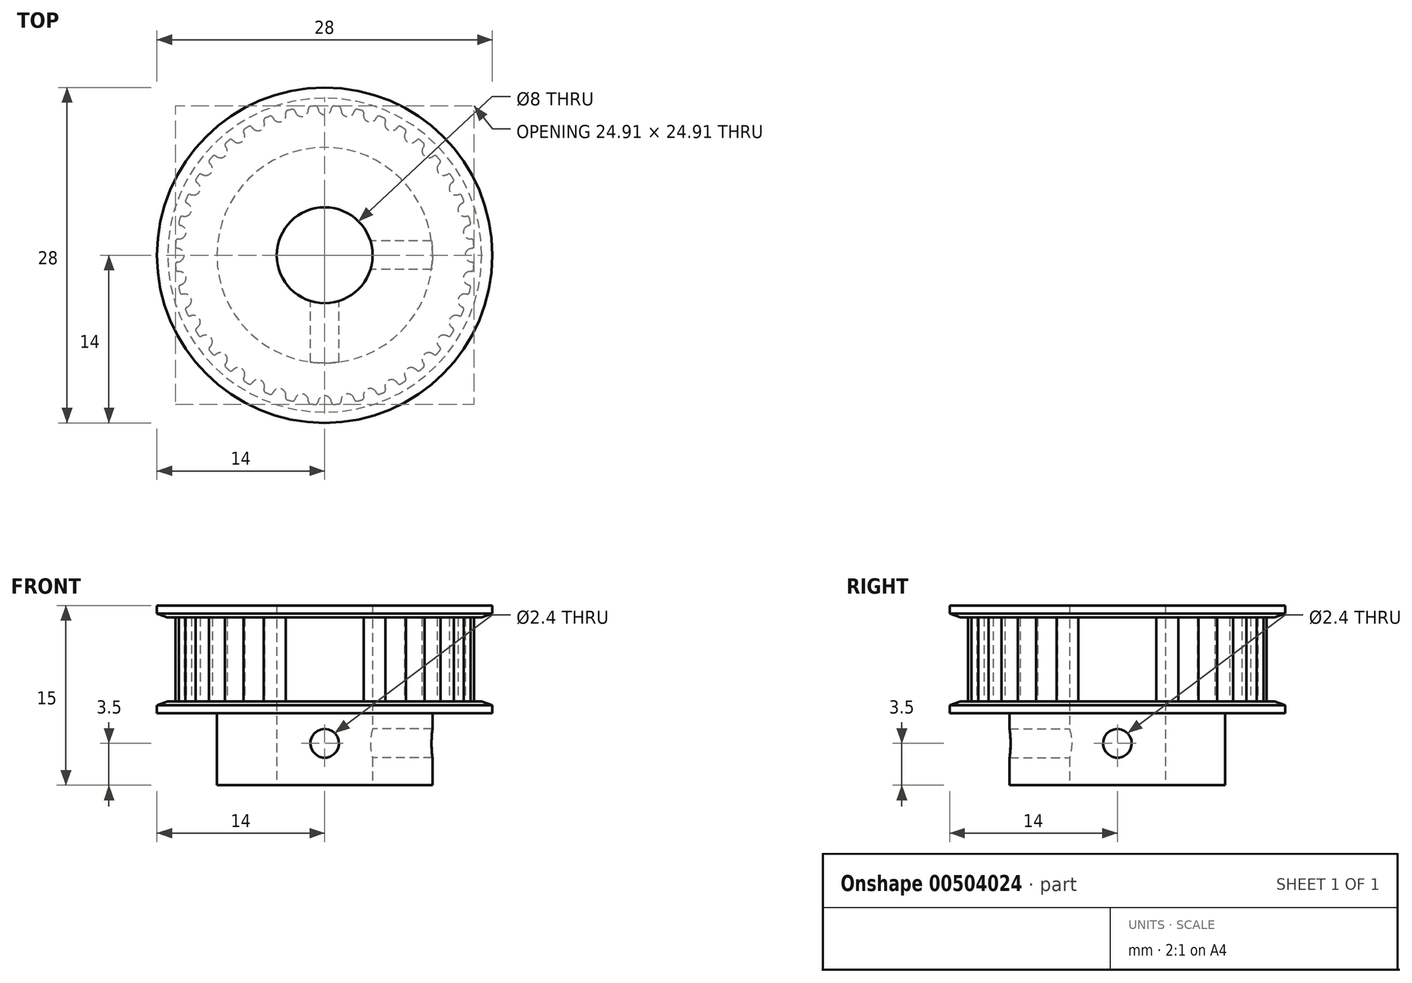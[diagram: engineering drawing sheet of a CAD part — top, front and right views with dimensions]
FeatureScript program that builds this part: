
annotation { "Feature Type Name" : "Feature", "Feature Type Description" : "" }
export const myFeature = defineFeature(function(context is Context, id is Id, definition is map)
    precondition{}
    {
        {
            assignVariable(context, id + "F0", {"name" : "teeth", "anyValue" : 40});
        }
        {
            assignVariable(context, id + "F1", {"name" : "belt_width", "anyValue" : 6 * mm});
        }
        {
            assignVariable(context, id + "F2", {"name" : "bore_diameter", "anyValue" : 8 * mm});
        }
        {
            var Q0;
            Q0=qCreatedBy(makeId("Top.planeOp"),FACE);
            var sketch = newSketch(context, id + "F3", { "sketchPlane" : qUnion([Q0])});
            skLineSegment(sketch, "E0", {"start": v(0, 0) * mm, "end": v(0, 11.73) * mm, "construction": true});
            skCircle(sketch, "E1", {"center": v(0, 0) * mm, "radius": 12.48 * mm});
            skPoint(sketch, "E2.MirrorCS.end.orphan", {"position": v(0.98, 12.44) * mm});
            skLineSegment(sketch, "E3", {"start": v(0.98, 12.44) * mm, "end": v(1, 12.7) * mm, "construction": true});
            skLineSegment(sketch, "E4", {"start": v(-0.98, 12.44) * mm, "end": v(-1, 12.7) * mm, "construction": true});
            skArc(sketch, "E5", {"start": v(0, 11.73) * mm, "mid": v(0.34, 11.84) * mm, "end": v(0.54, 12.14) * mm});
            skArc(sketch, "E6", {"start": v(0.54, 12.14) * mm, "mid": v(0.56, 12.23) * mm, "end": v(0.58, 12.33) * mm, "construction": true});
            skLineSegment(sketch, "E7", {"start": v(0, 11.73) * mm, "end": v(0, 12.48) * mm, "construction": true});
            skLineSegment(sketch, "E8", {"start": v(0, 12.48) * mm, "end": v(0, 12.73) * mm, "construction": true});
            skArc(sketch, "E9", {"start": v(0.58, 12.33) * mm, "mid": v(0.64, 12.42) * mm, "end": v(0.74, 12.46) * mm, "construction": true});
            skArc(sketch, "E10", {"start": v(1, 12.7) * mm, "mid": v(0, 12.73) * mm, "end": v(-1, 12.7) * mm, "construction": true});
            skLineSegment(sketch, "E11", {"start": v(0.98, 12.44) * mm, "end": v(0.92, 11.7) * mm});
            skLineSegment(sketch, "E12", {"start": v(0.92, 11.7) * mm, "end": v(0, 0) * mm});
            skLineSegment(sketch, "E13", {"start": v(0, 0) * mm, "end": v(-0.92, 11.7) * mm});
            skLineSegment(sketch, "E14", {"start": v(-0.92, 11.7) * mm, "end": v(-0.98, 12.44) * mm});
            skArc(sketch, "E15", {"start": v(0.77, 12.45) * mm, "mid": v(0.65, 12.42) * mm, "end": v(0.58, 12.31) * mm});
            skArc(sketch, "E16", {"start": v(0.54, 12.14) * mm, "mid": v(0.56, 12.22) * mm, "end": v(0.58, 12.31) * mm});
            skArc(sketch, "E17.MirrorCS", {"start": v(0, 11.73) * mm, "mid": v(-0.34, 11.84) * mm, "end": v(-0.54, 12.14) * mm});
            skArc(sketch, "E18.MirrorCS", {"start": v(-0.54, 12.14) * mm, "mid": v(-0.56, 12.22) * mm, "end": v(-0.58, 12.31) * mm});
            skArc(sketch, "E19.MirrorCS", {"start": v(-0.77, 12.45) * mm, "mid": v(-0.65, 12.42) * mm, "end": v(-0.58, 12.31) * mm});
            skArc(sketch, "E20", {"start": v(0, 12.48) * mm, "mid": v(-0.2, 12.48) * mm, "end": v(-0.4, 12.47) * mm});
            skArc(sketch, "E21", {"start": v(0.92, 11.7) * mm, "mid": v(0, 11.73) * mm, "end": v(-0.92, 11.7) * mm, "construction": true});
            skLineSegment(sketch, "E22", {"start": v(1, 12.7) * mm, "end": v(1.03, 13.07) * mm, "construction": true});
            skLineSegment(sketch, "E23", {"start": v(-1, 12.7) * mm, "end": v(-1.03, 13.07) * mm, "construction": true});
            skArc(sketch, "E24", {"start": v(-1.03, 13.07) * mm, "mid": v(0, 13.1) * mm, "end": v(1.03, 13.07) * mm, "construction": true});
            skSolve(sketch);
        }
        {
            var Q0;
            Q0=makeQuery(id+"F3.imprint","IMPRINT",FACE,{"disambiguationData":[TD([[makeQuery(id+"F3.imprint","IMPRINT",EDGE,{"derivedFrom":sQuery(id+"F3.wireOp",EDGE,"E5")}),-1.0]])]});
            var Q1;
            {var subQ1=sQuery(id+"F3.wireOp",EDGE,"E14");Q1=makeQuery(id+"F3.imprint","IMPRINT",FACE,{"disambiguationData":[TD([[makeQuery(id+"F3.imprint","IMPRINT",EDGE,{"derivedFrom":subQ1}),-1.0]])]});}
            var Q2;
            {var subQ0=sQuery(id+"F3.wireOp",EDGE,"E12");Q2=makeQuery(id+"F3.imprint","IMPRINT",FACE,{"disambiguationData":[TD([[makeQuery(id+"F3.imprint","IMPRINT",EDGE,{"derivedFrom":subQ0}),-1.0]])]});}
            extrude(context, id + "F4", {"entities" : qUnion([Q0, Q1, Q2]), "depth" : getVariable(context, 'belt_width') + 1 * mm, "symmetric" : true});
        }
        {
            var Q0;
            Q0=makeQuery(id+"F4.opExtrude","SWEPT_BODY",BODY,{"disambiguationData":[OSD([sQuery(id+"F3.wireOp",EDGE,"E1"),sQuery(id+"F3.wireOp",EDGE,"E5"),sQuery(id+"F3.wireOp",EDGE,"E11"),sQuery(id+"F3.wireOp",EDGE,"E12"),sQuery(id+"F3.wireOp",EDGE,"E13"),sQuery(id+"F3.wireOp",EDGE,"E14"),sQuery(id+"F3.wireOp",EDGE,"E15"),sQuery(id+"F3.wireOp",EDGE,"E16"),sQuery(id+"F3.wireOp",EDGE,"E17.MirrorCS"),sQuery(id+"F3.wireOp",EDGE,"E18.MirrorCS"),sQuery(id+"F3.wireOp",EDGE,"E19.MirrorCS")])]});
            var Q1;
            Q1=makeQuery(id+"F4.opExtrude","SWEPT_EDGE",EDGE,{"disambiguationData":[OSD([sQuery(id+"F3.wireOp",EDGE,"E12"),sQuery(id+"F3.wireOp",EDGE,"E13")])]});
            circularPattern(context, id + "F5", {"operationType" : NewBodyOperationType.ADD, "entities" : qUnion([Q0]), "axis" : qUnion([Q1]), "angle" : 360 * degree, "instanceCount" : getVariable(context, 'teeth'), "equalSpace" : true});
        }
        {
            var Q0;
            Q0=qCreatedBy(makeId("Front.planeOp"),FACE);
            var sketch = newSketch(context, id + "F6", { "sketchPlane" : qUnion([Q0])});
            skLineSegment(sketch, "E25", {"start": v(0, -3.5) * mm, "end": v(13.1, -3.5) * mm});
            skLineSegment(sketch, "E26", {"start": v(13.1, -3.5) * mm, "end": v(14, -3.82) * mm});
            skLineSegment(sketch, "E27", {"start": v(9, -10.5) * mm, "end": v(0, -10.5) * mm});
            skLineSegment(sketch, "E28", {"start": v(0, 3.5) * mm, "end": v(13.1, 3.5) * mm});
            skLineSegment(sketch, "E29", {"start": v(14, 3.82) * mm, "end": v(13.1, 3.5) * mm});
            skLineSegment(sketch, "E30", {"start": v(14, 3.82) * mm, "end": v(14, 4.5) * mm});
            skLineSegment(sketch, "E31", {"start": v(14, 4.5) * mm, "end": v(0, 4.5) * mm});
            skLineSegment(sketch, "E32", {"start": v(0, 4.5) * mm, "end": v(0, 3.5) * mm});
            skLineSegment(sketch, "E33", {"start": v(13.1, -3.5) * mm, "end": v(14, -3.5) * mm, "construction": true});
            skLineSegment(sketch, "E34", {"start": v(14, -3.5) * mm, "end": v(14, -3.82) * mm, "construction": true});
            skLineSegment(sketch, "E35", {"start": v(13.1, 3.5) * mm, "end": v(14, 3.5) * mm, "construction": true});
            skLineSegment(sketch, "E36", {"start": v(14, 3.5) * mm, "end": v(14, 3.82) * mm, "construction": true});
            skLineSegment(sketch, "E37", {"start": v(12.48, 0) * mm, "end": v(12.48, -3.5) * mm, "construction": true});
            skLineSegment(sketch, "E38", {"start": v(14, -4.5) * mm, "end": v(0, -4.5) * mm});
            skLineSegment(sketch, "E39", {"start": v(14, -3.82) * mm, "end": v(14, -4.5) * mm});
            skLineSegment(sketch, "E40", {"start": v(0, -3.5) * mm, "end": v(0, -4.5) * mm});
            skLineSegment(sketch, "E41", {"start": v(9, -10.5) * mm, "end": v(9, -4.5) * mm});
            skLineSegment(sketch, "E42", {"start": v(0, -10.5) * mm, "end": v(0, -4.5) * mm});
            skSolve(sketch);
        }
        {
            var Q0;
            Q0=makeQuery(id+"F6.imprint","IMPRINT",FACE,{"disambiguationData":[TD([[makeQuery(id+"F6.imprint","IMPRINT",EDGE,{"derivedFrom":sQuery(id+"F6.wireOp",EDGE,"E28")}),1.0]])]});
            var Q1;
            Q1=makeQuery(id+"F6.imprint","IMPRINT",FACE,{"disambiguationData":[TD([[makeQuery(id+"F6.imprint","IMPRINT",EDGE,{"derivedFrom":sQuery(id+"F6.wireOp",EDGE,"E25")}),-1.0]])]});
            var Q2;
            Q2=makeQuery(id+"F6.imprint","IMPRINT",FACE,{"disambiguationData":[TD([[makeQuery(id+"F6.imprint","IMPRINT",EDGE,{"derivedFrom":sQuery(id+"F6.wireOp",EDGE,"E27")}),-1.0]])]});
            var Q3;
            Q3=qConstructionFilter(qBodyType(qCreatedBy(id+"F6",EDGE),BodyType.WIRE),ConstructionObject.NO);
            var Q4;
            Q4=sQuery(id+"F6.wireOp",EDGE,"E42");
            revolve(context, id + "F7", {"operationType" : NewBodyOperationType.ADD, "entities" : qUnion([Q0, Q1, Q2]), "surfaceEntities" : qUnion([Q3]), "axis" : qUnion([Q4]), "revolveType" : RevolveType.FULL});
        }
        {
            var Q0;
            Q0=makeQuery(id+"F7.opRevolve","SWEPT_FACE",FACE,{"disambiguationData":[OSD([sQuery(id+"F6.wireOp",EDGE,"E27")])]});
            var sketch = newSketch(context, id + "F8", { "sketchPlane" : qUnion([Q0])});
            skPoint(sketch, "E43", {"position": v(0, 0) * mm});
            skSolve(sketch);
        }
        {
            var Q0;
            Q0=sQuery(id+"F8.wireOp",VERTEX,"E43");
            var Q1;
            Q1=makeQuery(id+"F4.opExtrude","SWEPT_BODY",BODY,{"disambiguationData":[OSD([sQuery(id+"F3.wireOp",EDGE,"E1"),sQuery(id+"F3.wireOp",EDGE,"E5"),sQuery(id+"F3.wireOp",EDGE,"E11"),sQuery(id+"F3.wireOp",EDGE,"E12"),sQuery(id+"F3.wireOp",EDGE,"E13"),sQuery(id+"F3.wireOp",EDGE,"E14"),sQuery(id+"F3.wireOp",EDGE,"E15"),sQuery(id+"F3.wireOp",EDGE,"E16"),sQuery(id+"F3.wireOp",EDGE,"E17.MirrorCS"),sQuery(id+"F3.wireOp",EDGE,"E18.MirrorCS"),sQuery(id+"F3.wireOp",EDGE,"E19.MirrorCS")])]});
            hole(context, id + "F9", {"style" : HoleStyle.SIMPLE, "holeDiameter" : getVariable(context, 'bore_diameter'), "endStyle" : HoleEndStyle.THROUGH, "locations" : qUnion([Q0]), "scope" : qUnion([Q1]), "isTappedThrough" : true});
        }
        {
            var Q0;
            Q0=qCreatedBy(makeId("Front.planeOp"),FACE);
            var sketch = newSketch(context, id + "F10", { "sketchPlane" : qUnion([Q0])});
            skPoint(sketch, "E44", {"position": v(0, -7) * mm});
            skLineSegment(sketch, "E45", {"start": v(0, -10.5) * mm, "end": v(0, -3.5) * mm});
            skSolve(sketch);
        }
        {
            var Q0;
            Q0=qCreatedBy(makeId("Right.planeOp"),FACE);
            var sketch = newSketch(context, id + "F11", { "sketchPlane" : qUnion([Q0])});
            skPoint(sketch, "E46", {"position": v(0, -7) * mm});
            skSolve(sketch);
        }
        {
            var Q0;
            Q0=sQuery(id+"F10.wireOp",VERTEX,"E44");
            var Q1;
            Q1=makeQuery(id+"F4.opExtrude","SWEPT_BODY",BODY,{"disambiguationData":[OSD([sQuery(id+"F3.wireOp",EDGE,"E1"),sQuery(id+"F3.wireOp",EDGE,"E5"),sQuery(id+"F3.wireOp",EDGE,"E11"),sQuery(id+"F3.wireOp",EDGE,"E12"),sQuery(id+"F3.wireOp",EDGE,"E13"),sQuery(id+"F3.wireOp",EDGE,"E14"),sQuery(id+"F3.wireOp",EDGE,"E15"),sQuery(id+"F3.wireOp",EDGE,"E16"),sQuery(id+"F3.wireOp",EDGE,"E17.MirrorCS"),sQuery(id+"F3.wireOp",EDGE,"E18.MirrorCS"),sQuery(id+"F3.wireOp",EDGE,"E19.MirrorCS")])]});
            hole(context, id + "F12", {"style" : HoleStyle.SIMPLE, "endStyle" : HoleEndStyle.THROUGH, "oppositeDirection" : true, "standardTappedOrClearance" : lookupTablePath({ "standard" : "ISO", "engagement" : "75%", "pitch" : "0.6 mm", "size" : "M3", "type" : "Tapped" }), "standardBlindInLast" : lookupTablePath({ "standard" : "ISO", "engagement" : "75%", "pitch" : "0.6 mm", "size" : "M3", "type" : "Tapped" }), "holeDiameter" : 2.4 * mm, "locations" : qUnion([Q0]), "scope" : qUnion([Q1]), "isTappedThrough" : true, "showTappedDepth" : true});
        }
        {
            var Q0;
            Q0=sQuery(id+"F11.wireOp",VERTEX,"E46");
            var Q1;
            Q1=makeQuery(id+"F4.opExtrude","SWEPT_BODY",BODY,{"disambiguationData":[OSD([sQuery(id+"F3.wireOp",EDGE,"E1"),sQuery(id+"F3.wireOp",EDGE,"E5"),sQuery(id+"F3.wireOp",EDGE,"E11"),sQuery(id+"F3.wireOp",EDGE,"E12"),sQuery(id+"F3.wireOp",EDGE,"E13"),sQuery(id+"F3.wireOp",EDGE,"E14"),sQuery(id+"F3.wireOp",EDGE,"E15"),sQuery(id+"F3.wireOp",EDGE,"E16"),sQuery(id+"F3.wireOp",EDGE,"E17.MirrorCS"),sQuery(id+"F3.wireOp",EDGE,"E18.MirrorCS"),sQuery(id+"F3.wireOp",EDGE,"E19.MirrorCS")])]});
            hole(context, id + "F13", {"style" : HoleStyle.SIMPLE, "endStyle" : HoleEndStyle.THROUGH, "oppositeDirection" : true, "standardTappedOrClearance" : lookupTablePath({ "standard" : "ISO", "engagement" : "75%", "pitch" : "0.6 mm", "size" : "M3", "type" : "Tapped" }), "standardBlindInLast" : lookupTablePath({ "standard" : "ISO", "engagement" : "75%", "pitch" : "0.6 mm", "size" : "M3", "type" : "Tapped" }), "holeDiameter" : 2.4 * mm, "locations" : qUnion([Q0]), "scope" : qUnion([Q1]), "isTappedThrough" : true, "showTappedDepth" : true});
        }
    });
